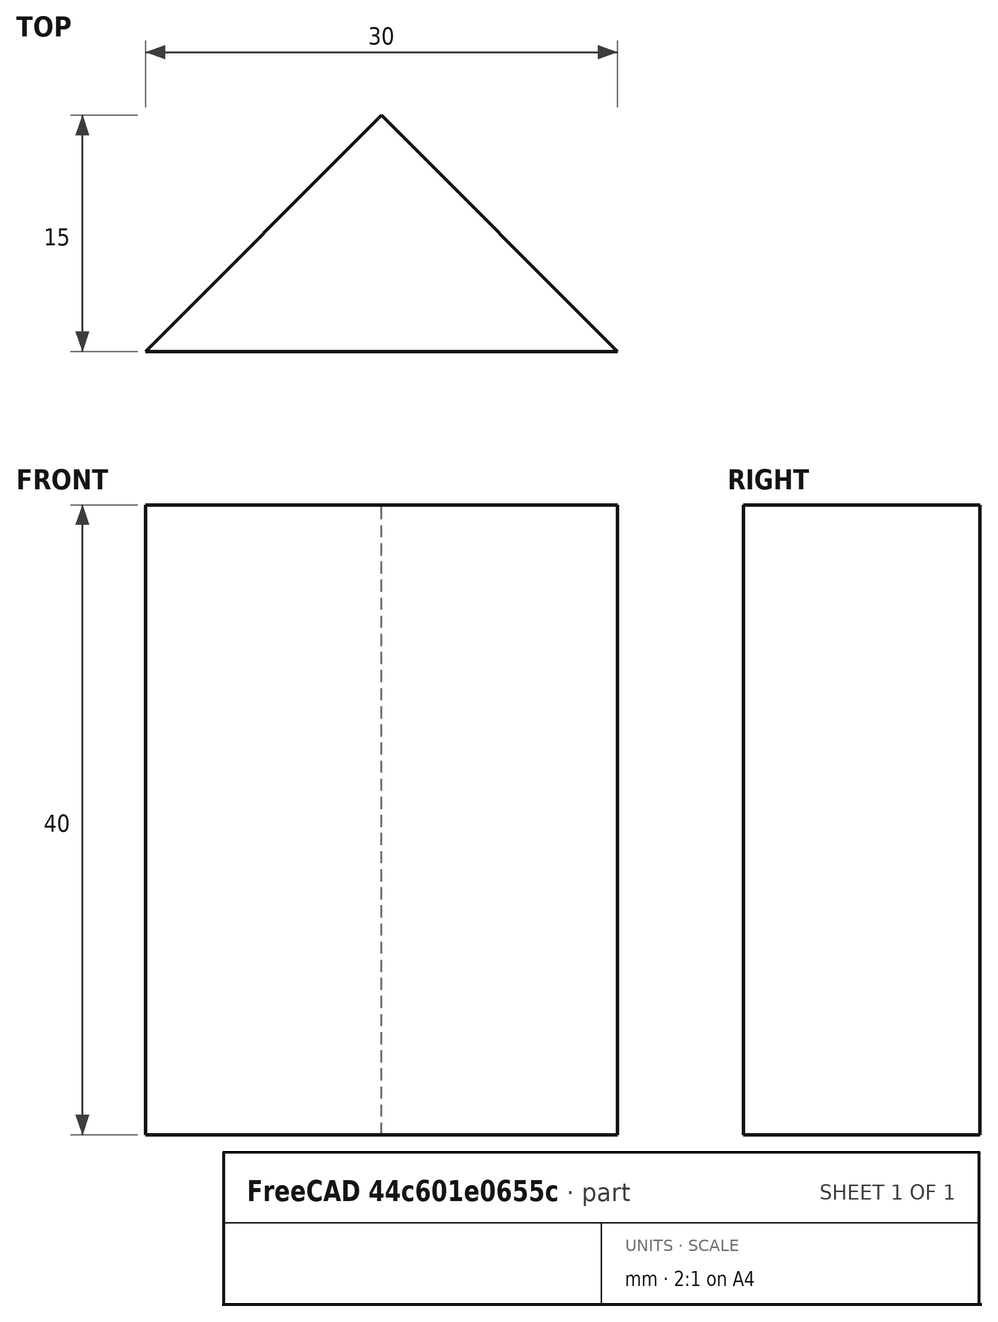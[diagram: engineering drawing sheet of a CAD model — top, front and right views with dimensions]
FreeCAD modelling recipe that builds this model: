
FCSTD DOCUMENT  (FreeCAD 0.20R29410 (Git))
Label: croquis5
License: Creative Commons Attribution-ShareAlike
LicenseURL: http://creativecommons.org/licenses/by-sa/4.0/
objects: Sketcher::SketchObject×1, Part::Extrusion×1
note: 2 computed .brp shape members not serialized (recipe doc carries the construction recipe); baked Part::Feature solids carry a one-line shape summary decoded from their .brp

FEATURE [Sketcher::SketchObject] Sketch
  FullyConstrained = true
  sketch-geometry (3):
    g0: LineSegment StartX=-15 StartY=0 StartZ=0 EndX=-1.8e-15 EndY=15 EndZ=0
    g1: LineSegment StartX=-1.8e-15 StartY=15 StartZ=0 EndX=15 EndY=0 EndZ=0
    g2: LineSegment StartX=15 StartY=0 StartZ=0 EndX=-15 EndY=0 EndZ=0
  constraints (8):
    c: PointOnObject(g0,g-1)
    c: PointOnObject(g0,g-2)
    c: Coincident(g0,g1)
    c: Coincident(g1,g2)
    c: Coincident(g2,g0)
    c: Symmetric(g0,g1,g-1)
    c: Angle(g2,g0) = 0.785398
    c: DistanceX(g2,g2) = 30
FEATURE [Part::Extrusion] Extrude
  Base = -> Sketch
  Dir = (0,0,1)
  DirMode = 2
  FaceMakerClass = Part::FaceMakerBullseye
  LengthFwd = 40
  LengthRev = 0
  Solid = true
  Symmetric = true
